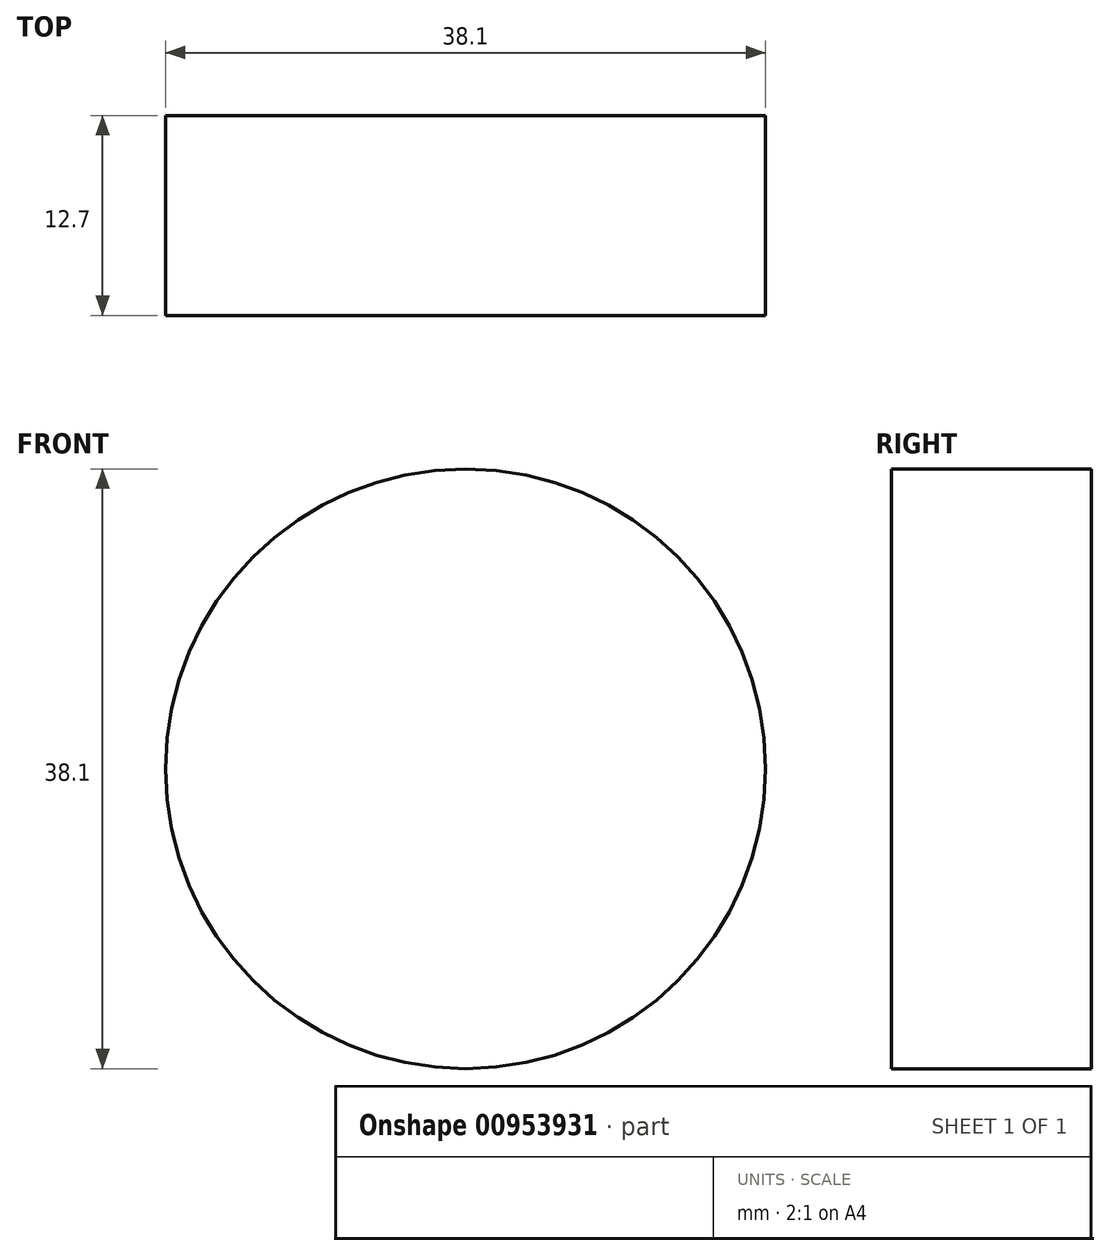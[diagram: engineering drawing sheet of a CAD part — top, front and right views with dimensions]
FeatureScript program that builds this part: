
annotation { "Feature Type Name" : "Feature", "Feature Type Description" : "" }
export const myFeature = defineFeature(function(context is Context, id is Id, definition is map)
    precondition{}
    {
        {
            var Q0;
            Q0=qCreatedBy(makeId("Front.planeOp"),FACE);
            var sketch = newSketch(context, id + "F0", { "sketchPlane" : qUnion([Q0])});
            skCircle(sketch, "E0", {"center": v(0, 2.3) * mm, "radius": 19.05 * mm});
            skSolve(sketch);
        }
        {
            var Q0;
            Q0=makeQuery(id+"F0.imprint","IMPRINT",FACE,{"disambiguationData":[TD([[makeQuery(id+"F0.imprint","IMPRINT",EDGE,{"derivedFrom":sQuery(id+"F0.wireOp",EDGE,"E0")}),1.0]])]});
            extrude(context, id + "F1", {"entities" : qUnion([Q0]), "depth" : 12.7 * mm, "offsetDistance" : 25.4 * mm});
        }
    });
